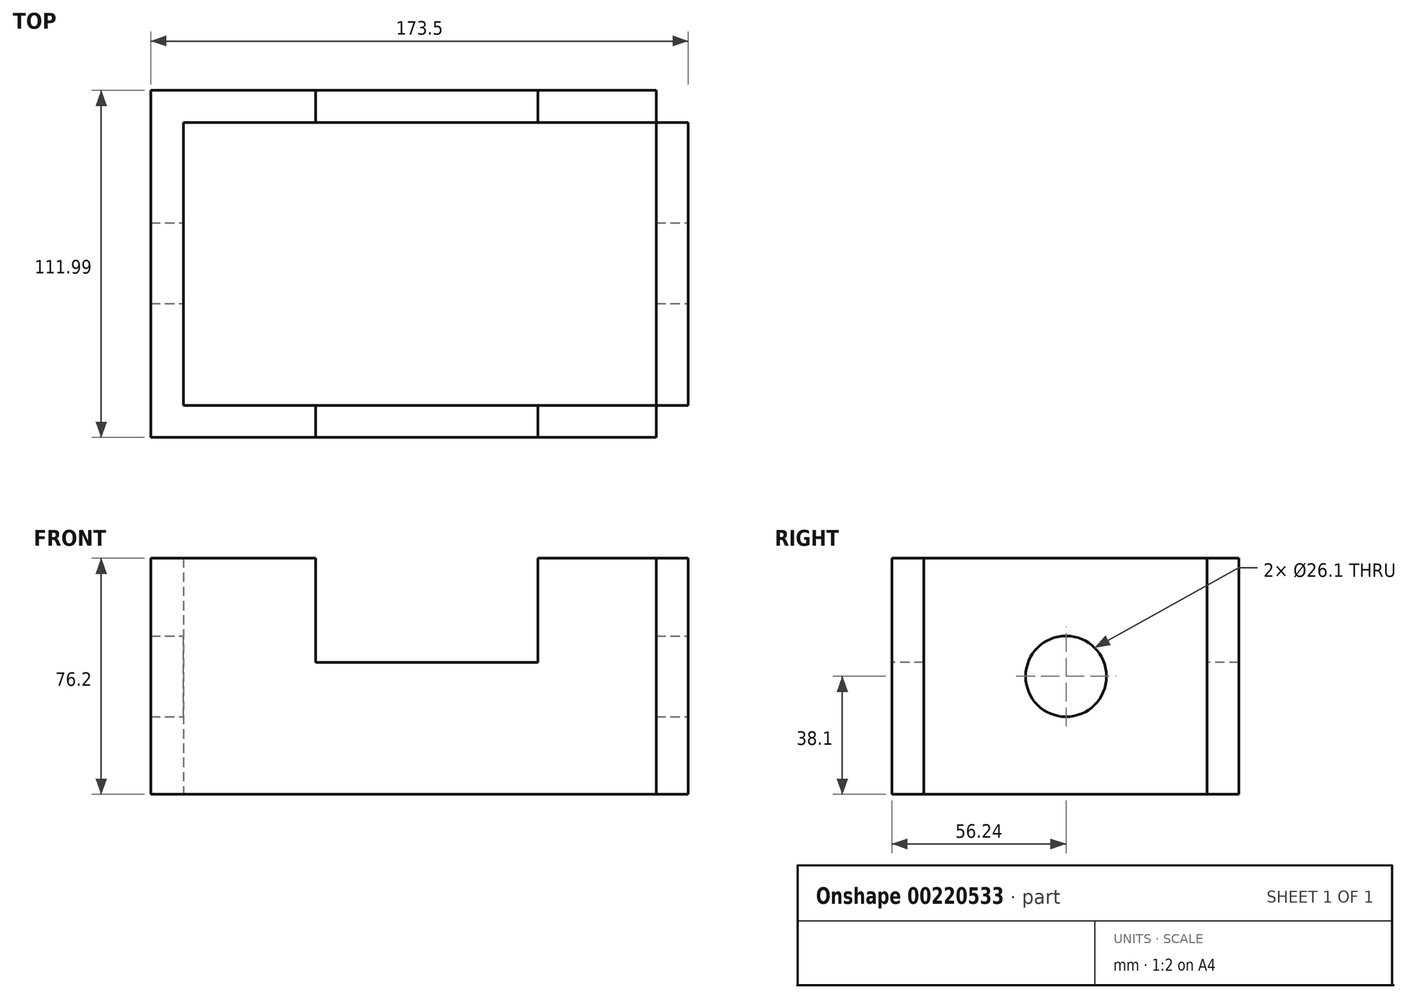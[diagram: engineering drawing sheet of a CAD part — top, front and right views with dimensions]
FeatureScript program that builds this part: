
annotation { "Feature Type Name" : "Feature", "Feature Type Description" : "" }
export const myFeature = defineFeature(function(context is Context, id is Id, definition is map)
    precondition{}
    {
        {
            var Q0;
            Q0=qCreatedBy(makeId("Top.planeOp"),FACE);
            var sketch = newSketch(context, id + "F0", { "sketchPlane" : qUnion([Q0])});
            skLineSegment(sketch, "E0.bottom", {"start": v(-76.21, 55.75) * mm, "end": v(-86.75, 55.75) * mm});
            skLineSegment(sketch, "E0.top", {"start": v(-76.21, -56.24) * mm, "end": v(-86.75, -56.24) * mm});
            skLineSegment(sketch, "E0.left", {"start": v(-76.21, 55.75) * mm, "end": v(-76.21, -56.24) * mm});
            skLineSegment(sketch, "E0.right", {"start": v(-86.75, 55.75) * mm, "end": v(-86.75, -56.24) * mm});
            skPoint(sketch, "E1.oppositeSnap0", {"position": v(-81.48, -56.24) * mm});
            skLineSegment(sketch, "E1.bottom", {"start": v(76.46, 56) * mm, "end": v(86.75, 56) * mm});
            skLineSegment(sketch, "E1.top", {"start": v(76.46, -56.24) * mm, "end": v(86.75, -56.24) * mm});
            skLineSegment(sketch, "E1.left", {"start": v(76.46, 56) * mm, "end": v(76.46, -56.24) * mm});
            skLineSegment(sketch, "E1.right", {"start": v(86.75, 56) * mm, "end": v(86.75, -56.24) * mm});
            skLineSegment(sketch, "E2.bottom", {"start": v(-86.75, 55.75) * mm, "end": v(86.75, 55.75) * mm});
            skLineSegment(sketch, "E2.top", {"start": v(-86.75, 45.46) * mm, "end": v(86.75, 45.46) * mm});
            skLineSegment(sketch, "E2.left", {"start": v(-86.75, 55.75) * mm, "end": v(-86.75, 45.46) * mm});
            skLineSegment(sketch, "E2.right", {"start": v(86.75, 55.75) * mm, "end": v(86.75, 45.46) * mm});
            skLineSegment(sketch, "E3.bottom", {"start": v(86.75, -56.24) * mm, "end": v(-86.75, -56.24) * mm});
            skLineSegment(sketch, "E3.top", {"start": v(86.75, -45.95) * mm, "end": v(-86.75, -45.95) * mm});
            skLineSegment(sketch, "E3.left", {"start": v(86.75, -56.24) * mm, "end": v(86.75, -45.95) * mm});
            skLineSegment(sketch, "E3.right", {"start": v(-86.75, -56.24) * mm, "end": v(-86.75, -45.95) * mm});
            skSolve(sketch);
        }
        {
            var Q0;
            {var subQ5=sQuery(id+"F0.wireOp",EDGE,"E0.right");Q0=makeQuery(id+"F0.imprint","IMPRINT",FACE,{"disambiguationData":[TD([[makeQuery(id+"F0.imprint","IMPRINT",EDGE,{"derivedFrom":subQ5}),1.0]])]});}
            var Q1;
            {var subQ0=sQuery(id+"F0.wireOp",EDGE,"E2.bottom");var subQ1=sQuery(id+"F0.wireOp",EDGE,"E0.left");var subQ2=makeQuery(id+"F0.imprint","INTERSECT",VERTEX,{"derivedFrom":[subQ1,subQ0]});Q1=makeQuery(id+"F0.imprint","IMPRINT",FACE,{"disambiguationData":[TD([[makeQuery(id+"F0.imprint","IMPRINT",EDGE,{"disambiguationData":[TD([[subQ2,-1.0]])],"derivedFrom":subQ1}),1.0]])]});}
            var Q2;
            {var subQ5=sQuery(id+"F0.wireOp",EDGE,"E2.left");Q2=makeQuery(id+"F0.imprint","IMPRINT",FACE,{"disambiguationData":[TD([[makeQuery(id+"F0.imprint","IMPRINT",EDGE,{"derivedFrom":subQ5}),1.0]])]});}
            var Q3;
            {var subQ5=sQuery(id+"F0.wireOp",EDGE,"E2.right");Q3=makeQuery(id+"F0.imprint","IMPRINT",FACE,{"disambiguationData":[TD([[makeQuery(id+"F0.imprint","IMPRINT",EDGE,{"derivedFrom":subQ5}),-1.0]])]});}
            var Q4;
            {var subQ0=sQuery(id+"F0.wireOp",EDGE,"E2.top");var subQ1=sQuery(id+"F0.wireOp",EDGE,"E1.left");var subQ2=makeQuery(id+"F0.imprint","INTERSECT",VERTEX,{"derivedFrom":[subQ1,subQ0]});Q4=makeQuery(id+"F0.imprint","IMPRINT",FACE,{"disambiguationData":[TD([[makeQuery(id+"F0.imprint","IMPRINT",EDGE,{"disambiguationData":[TD([[subQ2,-1.0]])],"derivedFrom":subQ1}),1.0]])]});}
            var Q5;
            {var subQ5=sQuery(id+"F0.wireOp",EDGE,"E3.left");Q5=makeQuery(id+"F0.imprint","IMPRINT",FACE,{"disambiguationData":[TD([[makeQuery(id+"F0.imprint","IMPRINT",EDGE,{"derivedFrom":subQ5}),1.0]])]});}
            var Q6;
            {var subQ0=sQuery(id+"F0.wireOp",EDGE,"E3.bottom");var subQ1=sQuery(id+"F0.wireOp",EDGE,"E0.left");var subQ2=makeQuery(id+"F0.imprint","INTERSECT",VERTEX,{"derivedFrom":[subQ1,subQ0]});Q6=makeQuery(id+"F0.imprint","IMPRINT",FACE,{"disambiguationData":[TD([[makeQuery(id+"F0.imprint","IMPRINT",EDGE,{"disambiguationData":[TD([[subQ2,1.0]])],"derivedFrom":subQ1}),1.0]])]});}
            var Q7;
            {var subQ5=sQuery(id+"F0.wireOp",EDGE,"E3.right");Q7=makeQuery(id+"F0.imprint","IMPRINT",FACE,{"disambiguationData":[TD([[makeQuery(id+"F0.imprint","IMPRINT",EDGE,{"derivedFrom":subQ5}),-1.0]])]});}
            extrude(context, id + "F1", {"entities" : qUnion([Q0, Q1, Q2, Q3, Q4, Q5, Q6, Q7]), "depth" : 76.2 * mm});
        }
        {
            var Q0;
            Q0=makeQuery(id+"F1.opExtrude","SWEPT_FACE",FACE,{"disambiguationData":[OSD([sQuery(id+"F0.wireOp",EDGE,"E3.bottom")])]});
            var sketch = newSketch(context, id + "F2", { "sketchPlane" : qUnion([Q0])});
            skLineSegment(sketch, "E4.bottom", {"start": v(0, 76.2) * mm, "end": v(38.24, 76.2) * mm});
            skLineSegment(sketch, "E4.top", {"start": v(0, 42.66) * mm, "end": v(38.24, 42.66) * mm});
            skLineSegment(sketch, "E4.left", {"start": v(0, 76.2) * mm, "end": v(0, 42.66) * mm});
            skLineSegment(sketch, "E4.right", {"start": v(38.24, 76.2) * mm, "end": v(38.24, 42.66) * mm});
            skLineSegment(sketch, "E5.bottom", {"start": v(0, 42.66) * mm, "end": v(-33.48, 42.66) * mm});
            skLineSegment(sketch, "E5.top", {"start": v(0, 76.2) * mm, "end": v(-33.48, 76.2) * mm});
            skLineSegment(sketch, "E5.left", {"start": v(0, 42.66) * mm, "end": v(0, 76.2) * mm});
            skLineSegment(sketch, "E5.right", {"start": v(-33.48, 42.66) * mm, "end": v(-33.48, 76.2) * mm});
            skSolve(sketch);
        }
        {
            var Q0;
            Q0=makeQuery(id+"F2.imprint","IMPRINT",FACE,{"disambiguationData":[TD([[makeQuery(id+"F2.imprint","IMPRINT",EDGE,{"derivedFrom":sQuery(id+"F2.wireOp",EDGE,"E4.bottom")}),1.0]])]});
            var Q1;
            Q1=makeQuery(id+"F2.imprint","IMPRINT",FACE,{"disambiguationData":[TD([[makeQuery(id+"F2.imprint","IMPRINT",EDGE,{"derivedFrom":sQuery(id+"F2.wireOp",EDGE,"E5.bottom")}),-1.0]])]});
            extrude(context, id + "F3", {"entities" : qUnion([Q0, Q1]), "operationType" : NewBodyOperationType.REMOVE, "endBound" : BoundingType.THROUGH_ALL, "oppositeDirection" : true, "depth" : 254 * mm});
        }
        {
            var Q0;
            Q0=makeQuery(id+"F1.opExtrude","SWEPT_FACE",FACE,{"disambiguationData":[OSD([sQuery(id+"F0.wireOp",EDGE,"E1.right"),sQuery(id+"F0.wireOp",EDGE,"E2.right"),sQuery(id+"F0.wireOp",EDGE,"E3.left")])]});
            var sketch = newSketch(context, id + "F4", { "sketchPlane" : qUnion([Q0])});
            skCircle(sketch, "E6", {"center": v(0, 38.1) * mm, "radius": 13.05 * mm});
            skPoint(sketch, "E6.centerSnap0", {"position": v(-56.24, 38.1) * mm});
            skSolve(sketch);
        }
        {
            var Q0;
            Q0=makeQuery(id+"F4.imprint","IMPRINT",FACE,{"disambiguationData":[TD([[makeQuery(id+"F4.imprint","IMPRINT",EDGE,{"derivedFrom":sQuery(id+"F4.wireOp",EDGE,"E6")}),1.0]])]});
            extrude(context, id + "F5", {"entities" : qUnion([Q0]), "operationType" : NewBodyOperationType.REMOVE, "endBound" : BoundingType.THROUGH_ALL, "oppositeDirection" : true, "depth" : 25.4 * mm});
        }
    });
